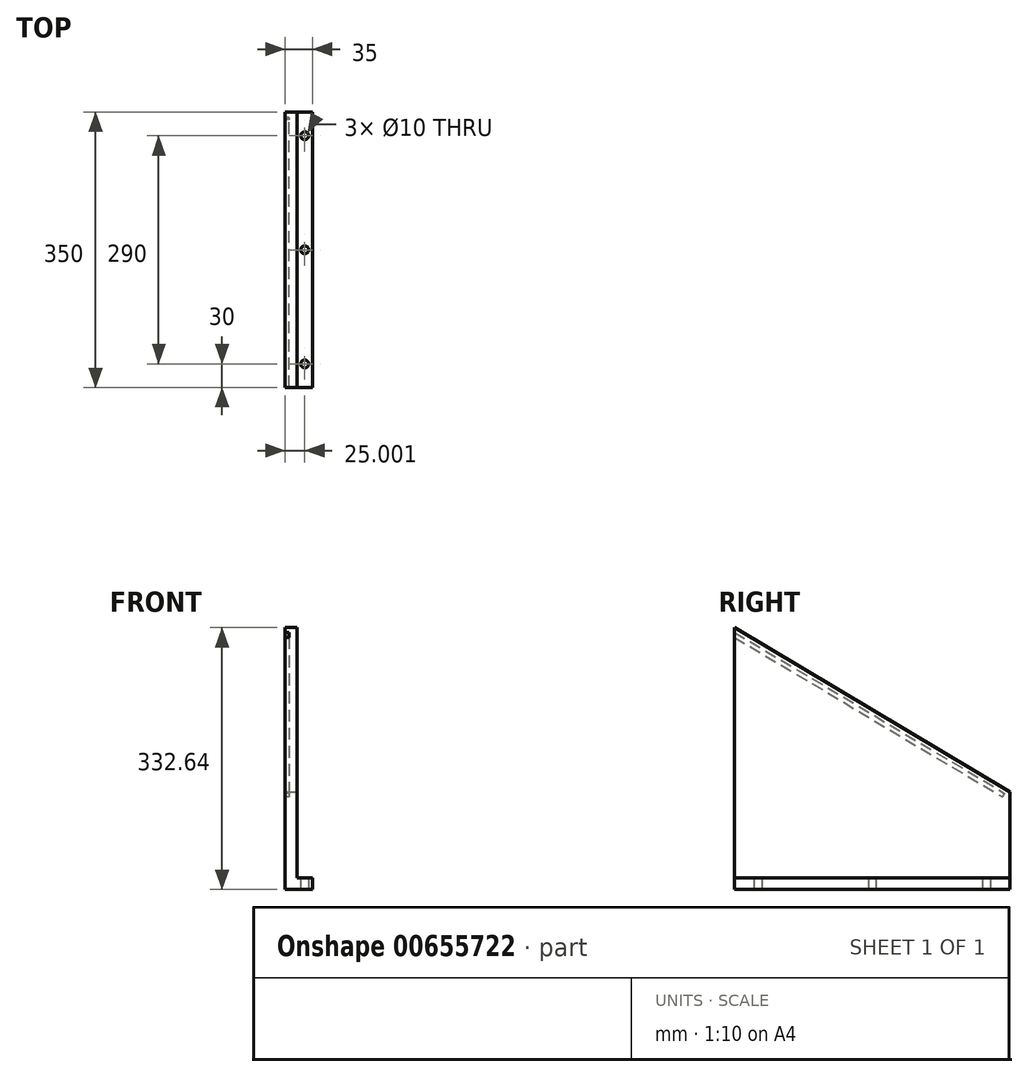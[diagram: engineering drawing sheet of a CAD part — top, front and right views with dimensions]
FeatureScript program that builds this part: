
annotation { "Feature Type Name" : "Feature", "Feature Type Description" : "" }
export const myFeature = defineFeature(function(context is Context, id is Id, definition is map)
    precondition{}
    {
        {
            var Q0;
            Q0=qCreatedBy(makeId("Top.planeOp"),FACE);
            var sketch = newSketch(context, id + "F0", { "sketchPlane" : qUnion([Q0])});
            skLineSegment(sketch, "E0.bottom", {"start": v(-75.23, -45.9) * mm, "end": v(-40.23, -45.9) * mm});
            skLineSegment(sketch, "E0.top", {"start": v(-75.23, 304.1) * mm, "end": v(-40.23, 304.1) * mm});
            skLineSegment(sketch, "E0.left", {"start": v(-75.23, -45.9) * mm, "end": v(-75.23, 304.1) * mm});
            skLineSegment(sketch, "E0.right", {"start": v(-40.23, -45.9) * mm, "end": v(-40.23, 304.1) * mm});
            skCircle(sketch, "E1", {"center": v(-50.23, -15.9) * mm, "radius": 5 * mm});
            skPoint(sketch, "E1.centerSnap0", {"position": v(-57.73, -45.9) * mm});
            skCircle(sketch, "E2", {"center": v(-50.23, 274.1) * mm, "radius": 5 * mm});
            skPoint(sketch, "E2.centerSnap0", {"position": v(-57.73, 304.1) * mm});
            skCircle(sketch, "E3", {"center": v(-50.23, 129.1) * mm, "radius": 5 * mm});
            skSolve(sketch);
        }
        {
            var Q0;
            Q0=qSketchRegion(id+"F0",true);
            extrude(context, id + "F1", {"entities" : qUnion([Q0]), "depth" : 15 * mm, "offsetDistance" : 25 * mm});
        }
        {
            var Q0;
            Q0=makeQuery(id+"F1.opExtrude","CAP_FACE",FACE,{"disambiguationData":[OSD([sQuery(id+"F0.wireOp",EDGE,"E0.bottom"),sQuery(id+"F0.wireOp",EDGE,"E0.top"),sQuery(id+"F0.wireOp",EDGE,"E0.left"),sQuery(id+"F0.wireOp",EDGE,"E0.right"),sQuery(id+"F0.wireOp",EDGE,"E1"),sQuery(id+"F0.wireOp",EDGE,"E2"),sQuery(id+"F0.wireOp",EDGE,"E3")])],"isStart":false});
            var sketch = newSketch(context, id + "F2", { "sketchPlane" : qUnion([Q0])});
            skLineSegment(sketch, "E4.bottom", {"start": v(-75.23, -45.9) * mm, "end": v(-60.23, -45.9) * mm});
            skLineSegment(sketch, "E4.top", {"start": v(-75.23, 304.1) * mm, "end": v(-60.23, 304.1) * mm});
            skLineSegment(sketch, "E4.left", {"start": v(-75.23, -45.9) * mm, "end": v(-75.23, 304.1) * mm});
            skLineSegment(sketch, "E4.right", {"start": v(-60.23, -45.9) * mm, "end": v(-60.23, 304.1) * mm});
            skSolve(sketch);
        }
        {
            var Q0;
            Q0=qSketchRegion(id+"F2",true);
            extrude(context, id + "F3", {"entities" : qUnion([Q0]), "operationType" : NewBodyOperationType.ADD, "depth" : 109 * mm, "offsetDistance" : 25 * mm});
        }
        {
            var Q0;
            Q0=makeQuery(id+"F3.opExtrude","SWEPT_FACE",FACE,{"disambiguationData":[OSD([sQuery(id+"F2.wireOp",EDGE,"E4.right")])]});
            var sketch = newSketch(context, id + "F4", { "sketchPlane" : qUnion([Q0])});
            skLineSegment(sketch, "E5", {"start": v(-45.9, 124) * mm, "end": v(304.1, 124) * mm});
            skLineSegment(sketch, "E6", {"start": v(-45.9, 124) * mm, "end": v(-45.9, 332.64) * mm});
            skLineSegment(sketch, "E7", {"start": v(-45.9, 332.64) * mm, "end": v(304.1, 124) * mm});
            skSolve(sketch);
        }
        {
            var Q0;
            Q0=qSketchRegion(id+"F4",true);
            extrude(context, id + "F5", {"entities" : qUnion([Q0]), "operationType" : NewBodyOperationType.ADD, "oppositeDirection" : true, "depth" : 15 * mm, "offsetDistance" : 25 * mm});
        }
        {
            var Q0;
            Q0=makeQuery(id+"F5.boolean.opBoolean","MERGE",FACE,{"derivedFrom":[makeQuery(id+"F3.boolean.opBoolean","MERGE",FACE,{"derivedFrom":[makeQuery(id+"F1.opExtrude","SWEPT_FACE",FACE,{"disambiguationData":[OSD([sQuery(id+"F0.wireOp",EDGE,"E0.left")])]}),makeQuery(id+"F3.opExtrude","SWEPT_FACE",FACE,{"disambiguationData":[OSD([sQuery(id+"F2.wireOp",EDGE,"E4.left")])]})]}),makeQuery(id+"F5.opExtrude","CAP_FACE",FACE,{"disambiguationData":[OSD([sQuery(id+"F4.wireOp",EDGE,"DwRSrHYv-oXvA-V4jq-Ijb4-9xwclgTuXcuy"),sQuery(id+"F4.wireOp",EDGE,"E5"),sQuery(id+"F4.wireOp",EDGE,"9Hu3hHWi-wN8L-nyCF-ANr8-TlmSygog2ZgI"),sQuery(id+"F4.wireOp",EDGE,"csEOVt2a-CrKH-hPNw-5nmC-xq5RosgazXYg")])],"isStart":false})]});
            var sketch = newSketch(context, id + "F6", { "sketchPlane" : qUnion([Q0])});
            skLineSegment(sketch, "E8.0", {"start": v(45.9, 326.82) * mm, "end": v(-297.24, 122.27) * mm});
            skLineSegment(sketch, "E9.0", {"start": v(45.9, 320.42) * mm, "end": v(-294.42, 117.54) * mm});
            skLineSegment(sketch, "E10.0", {"start": v(-297.24, 122.27) * mm, "end": v(-294.42, 117.54) * mm});
            skLineSegment(sketch, "E11", {"start": v(45.9, 326.82) * mm, "end": v(45.9, 320.42) * mm});
            skSolve(sketch);
        }
        {
            var Q0;
            Q0 = qSketchRegion(id + "F6", true);
            extrude(context, id + "F7", {"entities" : qUnion([Q0]), "operationType" : NewBodyOperationType.REMOVE, "oppositeDirection" : true, "depth" : 5 * mm, "offsetDistance" : 25 * mm});
        }
    });
